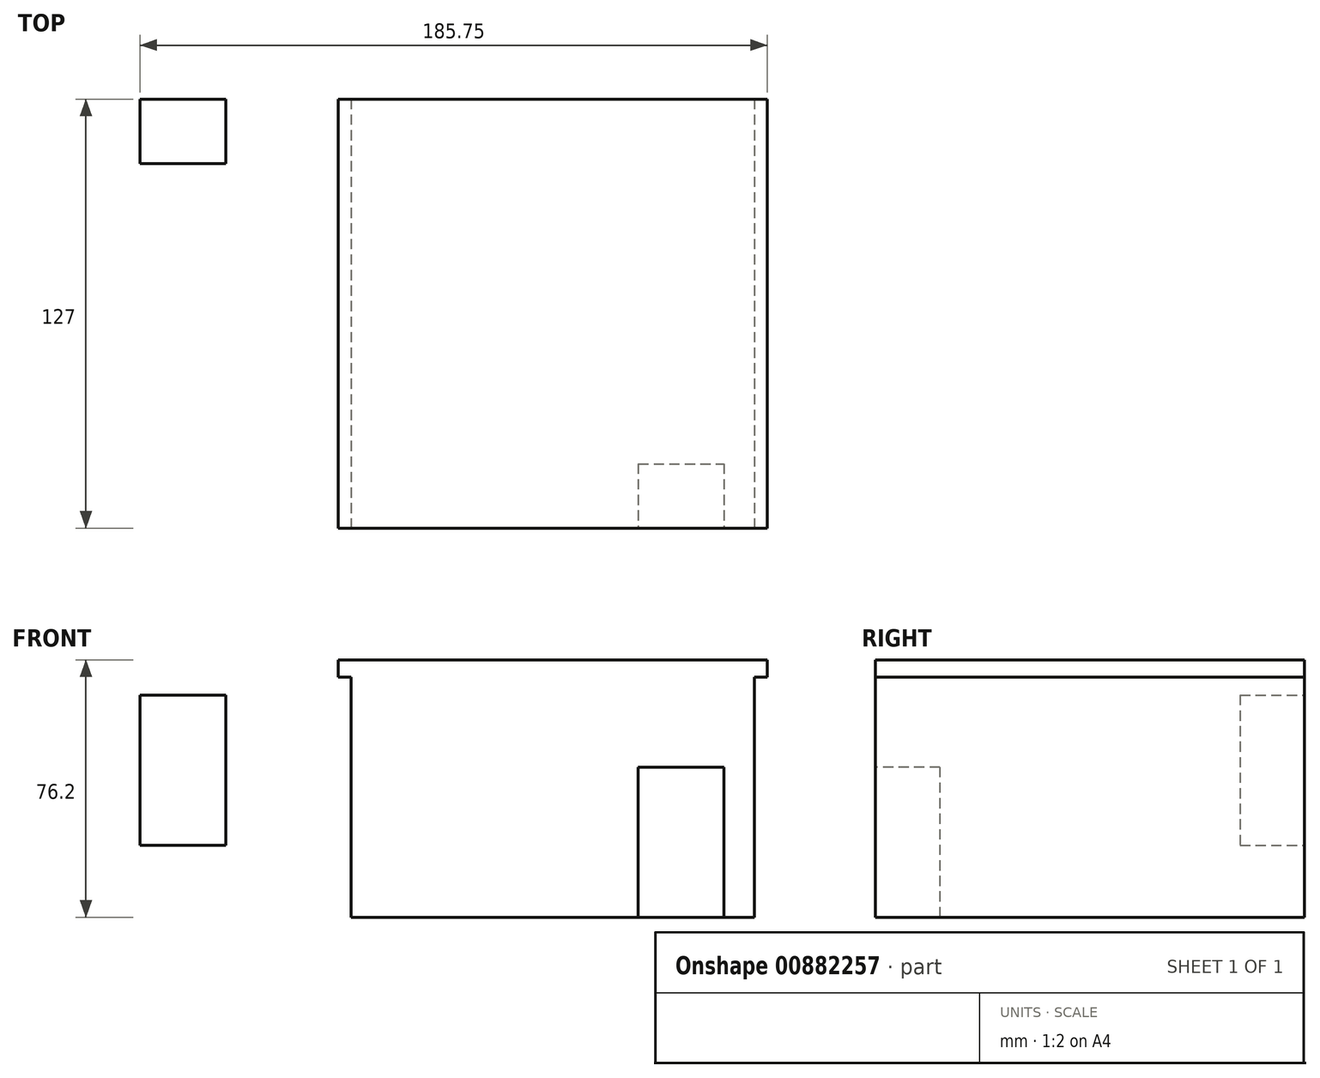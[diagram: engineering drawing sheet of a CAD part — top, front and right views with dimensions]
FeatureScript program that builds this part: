
annotation { "Feature Type Name" : "Feature", "Feature Type Description" : "" }
export const myFeature = defineFeature(function(context is Context, id is Id, definition is map)
    precondition{}
    {
        {
            var Q0;
            Q0=qCreatedBy(makeId("Front.planeOp"),FACE);
            var sketch = newSketch(context, id + "F0", { "sketchPlane" : qUnion([Q0])});
            skLineSegment(sketch, "E0.bottom", {"start": v(-62.83, 38.78) * mm, "end": v(64.17, 38.78) * mm});
            skLineSegment(sketch, "E0.top", {"start": v(-62.83, -37.42) * mm, "end": v(64.17, -37.42) * mm});
            skLineSegment(sketch, "E0.left", {"start": v(-62.83, 38.78) * mm, "end": v(-62.83, -37.42) * mm});
            skLineSegment(sketch, "E0.right", {"start": v(64.17, 38.78) * mm, "end": v(64.17, -37.42) * mm});
            skSolve(sketch);
        }
        {
            var Q0;
            Q0=makeQuery(id+"F0.imprint","IMPRINT",FACE,{"disambiguationData":[TD([[makeQuery(id+"F0.imprint","IMPRINT",EDGE,{"derivedFrom":sQuery(id+"F0.wireOp",EDGE,"E0.bottom")}),-1.0]])]});
            extrude(context, id + "F1", {"entities" : qUnion([Q0]), "depth" : 127 * mm, "offsetDistance" : 25.4 * mm});
        }
        {
            var Q0;
            Q0=makeQuery(id+"F1.opExtrude","CAP_FACE",FACE,{"disambiguationData":[OSD([sQuery(id+"F0.wireOp",EDGE,"E0.bottom"),sQuery(id+"F0.wireOp",EDGE,"E0.top"),sQuery(id+"F0.wireOp",EDGE,"E0.left"),sQuery(id+"F0.wireOp",EDGE,"E0.right")])],"isStart":false});
            var sketch = newSketch(context, id + "F2", { "sketchPlane" : qUnion([Q0])});
            skLineSegment(sketch, "E1.bottom", {"start": v(25.94, 7.03) * mm, "end": v(51.34, 7.03) * mm});
            skLineSegment(sketch, "E1.top", {"start": v(25.94, -37.42) * mm, "end": v(51.34, -37.42) * mm});
            skLineSegment(sketch, "E1.left", {"start": v(25.94, 7.03) * mm, "end": v(25.94, -37.42) * mm});
            skLineSegment(sketch, "E1.right", {"start": v(51.34, 7.03) * mm, "end": v(51.34, -37.42) * mm});
            skSolve(sketch);
        }
        {
            var Q0;
            Q0=makeQuery(id+"F2.imprint","IMPRINT",FACE,{"disambiguationData":[TD([[makeQuery(id+"F2.imprint","IMPRINT",EDGE,{"derivedFrom":sQuery(id+"F2.wireOp",EDGE,"E1.bottom")}),-1.0]])]});
            extrude(context, id + "F3", {"entities" : qUnion([Q0]), "operationType" : NewBodyOperationType.REMOVE, "oppositeDirection" : true, "depth" : 19.05 * mm, "offsetDistance" : 25.4 * mm});
        }
        {
            var Q0;
            Q0=qCreatedBy(makeId("Front.planeOp"),FACE);
            var sketch = newSketch(context, id + "F4", { "sketchPlane" : qUnion([Q0])});
            skLineSegment(sketch, "E2.bottom", {"start": v(-121.58, 28.36) * mm, "end": v(-96.18, 28.36) * mm});
            skLineSegment(sketch, "E2.top", {"start": v(-121.58, -16.1) * mm, "end": v(-96.18, -16.1) * mm});
            skLineSegment(sketch, "E2.left", {"start": v(-121.58, 28.36) * mm, "end": v(-121.58, -16.1) * mm});
            skLineSegment(sketch, "E2.right", {"start": v(-96.18, 28.36) * mm, "end": v(-96.18, -16.1) * mm});
            skSolve(sketch);
        }
        {
            var Q0;
            Q0=makeQuery(id+"F4.imprint","IMPRINT",FACE,{"disambiguationData":[TD([[makeQuery(id+"F4.imprint","IMPRINT",EDGE,{"derivedFrom":sQuery(id+"F4.wireOp",EDGE,"E2.bottom")}),-1.0]])]});
            extrude(context, id + "F5", {"entities" : qUnion([Q0]), "depth" : 19.05 * mm, "offsetDistance" : 25.4 * mm});
        }
        {
            var Q0;
            Q0=makeQuery(id+"F1.opExtrude","CAP_FACE",FACE,{"disambiguationData":[OSD([sQuery(id+"F0.wireOp",EDGE,"E0.bottom"),sQuery(id+"F0.wireOp",EDGE,"E0.top"),sQuery(id+"F0.wireOp",EDGE,"E0.left"),sQuery(id+"F0.wireOp",EDGE,"E0.right")])],"isStart":false});
            var sketch = newSketch(context, id + "F6", { "sketchPlane" : qUnion([Q0])});
            skLineSegment(sketch, "E3.bottom", {"start": v(-62.83, 33.7) * mm, "end": v(-59.02, 33.7) * mm});
            skLineSegment(sketch, "E3.top", {"start": v(-62.83, -37.42) * mm, "end": v(-59.02, -37.42) * mm});
            skLineSegment(sketch, "E3.left", {"start": v(-62.83, 33.7) * mm, "end": v(-62.83, -37.42) * mm});
            skLineSegment(sketch, "E3.right", {"start": v(-59.02, 33.7) * mm, "end": v(-59.02, -37.42) * mm});
            skSolve(sketch);
        }
        {
            var Q0;
            Q0=makeQuery(id+"F6.imprint","IMPRINT",FACE,{"disambiguationData":[TD([[makeQuery(id+"F6.imprint","IMPRINT",EDGE,{"derivedFrom":sQuery(id+"F6.wireOp",EDGE,"E3.bottom")}),-1.0]])]});
            extrude(context, id + "F7", {"entities" : qUnion([Q0]), "operationType" : NewBodyOperationType.REMOVE, "oppositeDirection" : true, "depth" : 127 * mm, "offsetDistance" : 25.4 * mm});
        }
        {
            var Q0;
            Q0=makeQuery(id+"F1.opExtrude","CAP_FACE",FACE,{"disambiguationData":[OSD([sQuery(id+"F0.wireOp",EDGE,"E0.bottom"),sQuery(id+"F0.wireOp",EDGE,"E0.top"),sQuery(id+"F0.wireOp",EDGE,"E0.left"),sQuery(id+"F0.wireOp",EDGE,"E0.right")])],"isStart":false});
            var sketch = newSketch(context, id + "F8", { "sketchPlane" : qUnion([Q0])});
            skLineSegment(sketch, "E4.bottom", {"start": v(64.17, 33.7) * mm, "end": v(60.36, 33.7) * mm});
            skLineSegment(sketch, "E4.top", {"start": v(64.17, -37.42) * mm, "end": v(60.36, -37.42) * mm});
            skLineSegment(sketch, "E4.left", {"start": v(64.17, 33.7) * mm, "end": v(64.17, -37.42) * mm});
            skLineSegment(sketch, "E4.right", {"start": v(60.36, 33.7) * mm, "end": v(60.36, -37.42) * mm});
            skSolve(sketch);
        }
        {
            var Q0;
            Q0 = qSketchRegion(id + "F8", true);
            extrude(context, id + "F9", {"entities" : qUnion([Q0]), "operationType" : NewBodyOperationType.REMOVE, "oppositeDirection" : true, "depth" : 127 * mm, "offsetDistance" : 25.4 * mm});
        }
    });
